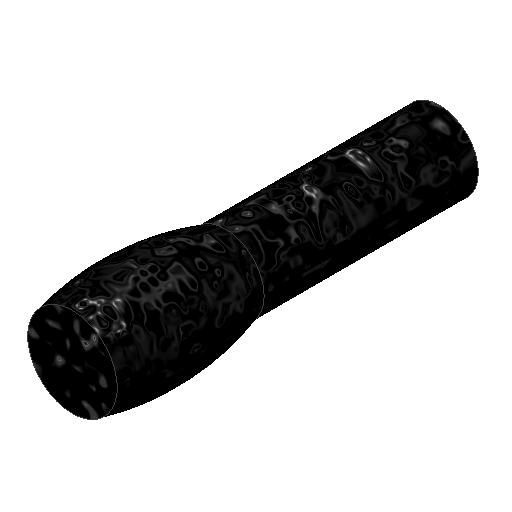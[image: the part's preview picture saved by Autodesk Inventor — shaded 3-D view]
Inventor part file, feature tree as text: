
AUTODESK INVENTOR PART (.ipt)
format: ipt  version: 2022 (Build 260153000, 153)  size: 156,672 bytes
history: native  units: mm
features: sketch x2, extrude x1, revolve x1
ambient origin geometry x8: Origin, YZ Plane, XZ Plane, XY Plane, X Axis, Y Axis, Z Axis, Center Point
bodies: Volumenkörper1 (feature_tree)
feature tree (4):
  extrude  "Extrusion1"  Depth=77.0mm TaperAngle=0.0deg
  revolve  "Umdrehung1"
  sketch  "Skizze1"  dims[d0=27.9mm d1=77.0mm d2=0.0mm]
  sketch  "Skizze2"  dims[d3=55.0mm d4=18.925mm d5=90.0deg d6=16.085mm]
